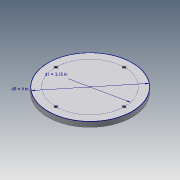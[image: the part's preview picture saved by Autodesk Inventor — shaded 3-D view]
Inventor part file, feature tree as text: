
AUTODESK INVENTOR PART (.ipt)
format: ipt  version: 2020.3 (Build 243373000, 373)  size: 100,352 bytes
history: native  units: in
note: dims shown in document units (in); Inventor stores cm internally (conversion verified against a paired STEP export)
features: sketch x1, extrude x1, hole x1
ambient origin geometry x8: Origin, YZ Plane, XZ Plane, XY Plane, X Axis, Y Axis, Z Axis, Center Point
bodies: Solid1 (feature_tree)
feature tree (3):
  sketch  "Sketch1"  dims[d0=4.0in d1=3.25in d2=0.25in d3=0.0in d4=0.1276in d5=0.315in d6=0.375in d7=0.25in d8=0.5635in d9=0.465in d10=0.8108in]
  extrude  "Extrusion1"  Depth=0.25in
  hole  "Hole1"  [1 undecoded]
note: 1 required parameter value undecoded (feature->parameter linkage not recoverable at this tier; creation-order binding heuristic only, values carry confidence <= 0.55)
